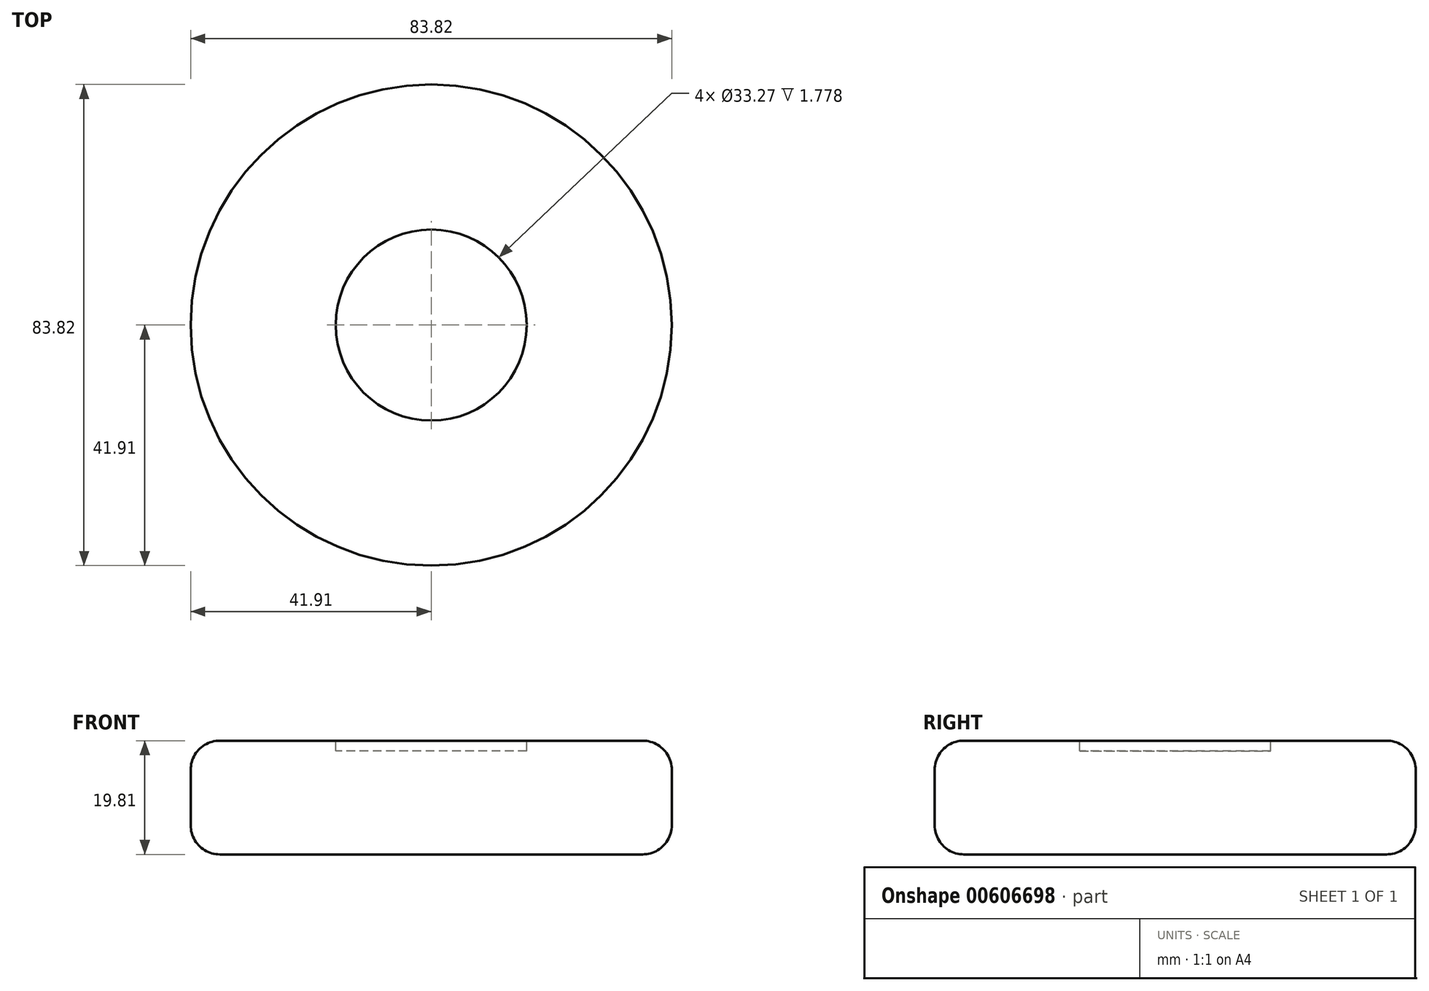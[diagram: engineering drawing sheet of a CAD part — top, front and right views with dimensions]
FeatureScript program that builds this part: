
annotation { "Feature Type Name" : "Feature", "Feature Type Description" : "" }
export const myFeature = defineFeature(function(context is Context, id is Id, definition is map)
    precondition{}
    {
        {
            var Q0;
            Q0=qCreatedBy(makeId("Top.planeOp"),FACE);
            var sketch = newSketch(context, id + "F0", { "sketchPlane" : qUnion([Q0])});
            skCircle(sketch, "E0", {"center": v(0, 0) * mm, "radius": 41.91 * mm});
            skSolve(sketch);
        }
        {
            var Q0;
            Q0 = qSketchRegion(id + "F0", true);
            extrude(context, id + "F1", {"entities" : qUnion([Q0]), "depth" : 19.8 * mm, "offsetDistance" : 25.4 * mm});
        }
        {
            var Q0;
            Q0=makeQuery(id+"F1.opExtrude","CAP_FACE",FACE,{"disambiguationData":[OSD([sQuery(id+"F0.wireOp",EDGE,"E0")])],"isStart":false});
            var sketch = newSketch(context, id + "F2", { "sketchPlane" : qUnion([Q0])});
            skCircle(sketch, "E1", {"center": v(0, 0) * mm, "radius": 16.64 * mm});
            skSolve(sketch);
        }
        {
            var Q0;
            Q0 = qSketchRegion(id + "F2", true);
            extrude(context, id + "F3", {"entities" : qUnion([Q0]), "operationType" : NewBodyOperationType.REMOVE, "oppositeDirection" : true, "depth" : 1.78 * mm, "offsetDistance" : 25.4 * mm});
        }
        {
            var Q0;
            Q0=makeQuery(id+"F1.opExtrude","CAP_EDGE",EDGE,{"disambiguationData":[OSD([sQuery(id+"F0.wireOp",EDGE,"E0")])],"isStart":true});
            var Q1;
            Q1=makeQuery(id+"F1.opExtrude","CAP_EDGE",EDGE,{"disambiguationData":[OSD([sQuery(id+"F0.wireOp",EDGE,"E0")])],"isStart":false});
            fillet(context, id + "F4", {"entities" : qUnion([Q0, Q1]), "radius" : 5.08 * mm, "tangentPropagation" : true, "allowEdgeOverflow" : false});
        }
    });
